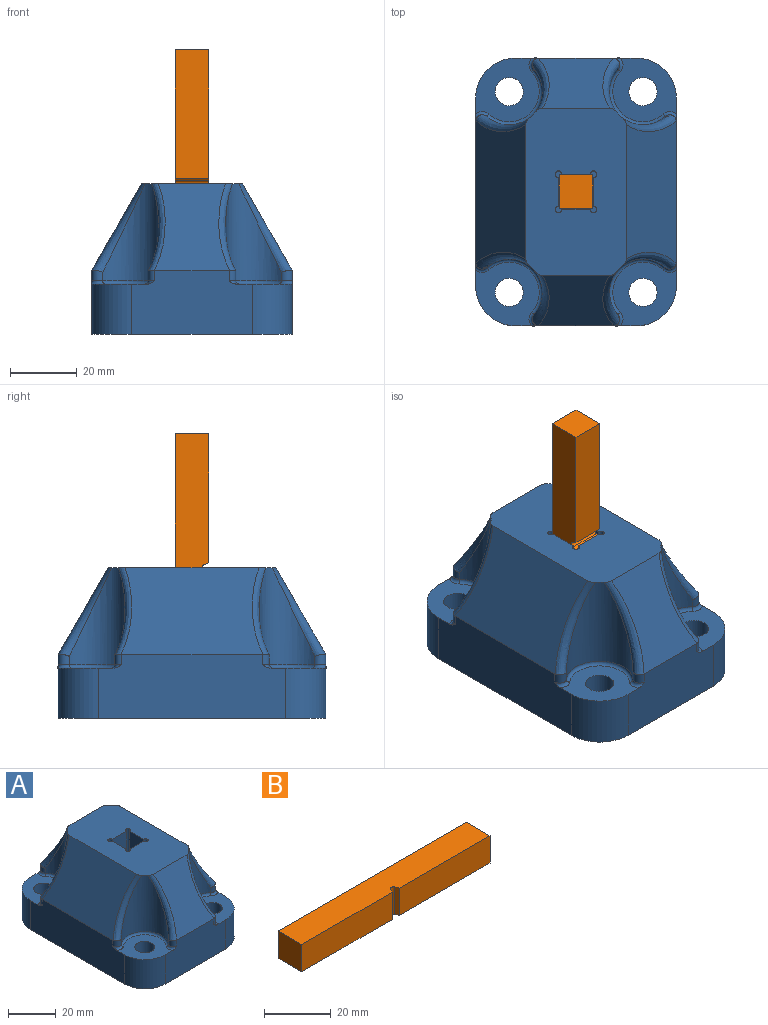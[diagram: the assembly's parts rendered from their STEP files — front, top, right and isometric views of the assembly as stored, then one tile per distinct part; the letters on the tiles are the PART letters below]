
ASSEMBLY  parts=2 mates=1
PART A: 63 faces, bbox 64.3x84.3x46.3 mm
  f0: plane 25.99x22.59mm, normal (0,0.87,0.5), area 532mm2, adj f10,f13,f35,f36,f39,f40
  f1: plane 42.59x25.99mm, normal (-0.87,0,0.5), area 1132mm2, adj f10,f11,f37,f38,f49,f50
  f2: cylinder r=12mm len=15mm, axis (0,0,-1), area 282.7mm2, adj f8,f11,f13,f33
  f3: plane 42.59x25.99mm, normal (0.87,0,0.5), area 1132mm2, adj f9,f10,f41,f42,f45,f46
  f4: cylinder r=12mm len=15mm, axis (0,0,1), area 282.7mm2, adj f8,f9,f13,f30
  f5: plane 25.99x22.59mm, normal (0,-0.87,0.5), area 532mm2, adj f10,f12,f43,f44,f47,f48
  f6: cylinder r=12mm len=15mm, axis (0,0,-1), area 282.7mm2, adj f8,f9,f12,f27
  f7: cylinder r=12mm len=15mm, axis (0,0,1), area 282.7mm2, adj f8,f11,f12,f24
  f8: plane 80x60mm, normal (0,0,-1), area 4454.7mm2, adj f2,f4,f6,f7,f9,f11,f12,f13
  f9: plane 56.31x19.33mm, normal (1,0,0), area 1010.9mm2, adj f3,f4,f6,f8,f27,f30,f41,f45
  f10: plane 50.19x30.19mm, normal (0,0,1), area 1346.6mm2, adj f0,f1,f3,f5,f14,f15,f16,f17
  f11: plane 56.31x19.33mm, normal (-1,0,0), area 1010.9mm2, adj f1,f2,f7,f8,f24,f33,f37,f49
  f12: plane 36.31x19.33mm, normal (0,-1,0), area 630.5mm2, adj f5,f6,f7,f8,f24,f27,f43,f47
  f13: plane 36.31x19.33mm, normal (0,1,0), area 630.5mm2, adj f0,f2,f4,f8,f30,f33,f35,f39
  f14: cylinder r=1mm len=40mm, axis (0,0,1), area 188.5mm2, adj f10,f15,f21,f22
  f15: plane 40x8.5mm, normal (1,0,0), area 340mm2, adj f10,f14,f16,f22
  f16: cylinder r=1mm len=40mm, axis (0,0,1), area 188.5mm2, adj f10,f15,f17,f22
  f17: plane 40x8.5mm, normal (0,1,0), area 340mm2, adj f10,f16,f18,f22
  f18: cylinder r=1mm len=40mm, axis (0,0,1), area 188.5mm2, adj f10,f17,f19,f22
  f19: plane 40x8.5mm, normal (-1,0,0), area 340mm2, adj f10,f18,f20,f22
  f20: cylinder r=1mm len=40mm, axis (0,0,1), area 188.5mm2, adj f10,f19,f21,f22
  f21: plane 40x8.5mm, normal (0,-1,0), area 340mm2, adj f10,f14,f20,f22
  f22: plane 12.5x12.5mm, normal (0,0,1), area 119.7mm2, adj f14,f15,f16,f17,f18,f19,f20,f21
  f23: cylinder r=4.2mm len=15mm, axis (0,0,1), area 395.8mm2, adj f8,f24
  f24: plane 19x19mm, normal (0,0,1), area 226.1mm2, adj f7,f11,f12,f23,f51,f52,f53
  f25: cylinder r=10mm len=29mm, axis (0,0,1), area 511.6mm2, adj f10,f47,f48,f49,f50,f52
  f26: cylinder r=4.2mm len=15mm, axis (0,0,1), area 395.8mm2, adj f8,f27
  f27: plane 19x19mm, normal (0,0,1), area 226.1mm2, adj f6,f9,f12,f26,f54,f55,f56
  f28: cylinder r=10mm len=29mm, axis (0,0,1), area 511.6mm2, adj f10,f43,f44,f45,f46,f55
  f29: cylinder r=4.2mm len=15mm, axis (0,0,1), area 395.8mm2, adj f8,f30
  f30: plane 19x19mm, normal (0,0,1), area 226.1mm2, adj f4,f9,f13,f29,f57,f58,f59
  f31: cylinder r=10mm len=29mm, axis (0,0,1), area 511.6mm2, adj f10,f39,f40,f41,f42,f58
  f32: cylinder r=4.2mm len=15mm, axis (0,0,1), area 395.8mm2, adj f8,f33
  f33: plane 19x19mm, normal (0,0,1), area 226.1mm2, adj f2,f11,f13,f32,f60,f61,f62
  f34: cylinder r=10mm len=29mm, axis (0,0,1), area 511.6mm2, adj f10,f35,f36,f37,f38,f61
  f35: cylinder r=2mm len=3.33mm, axis (0,0,1), area 13.7mm2, adj f0,f13,f34,f36,f60
  f36: bspline ~28.08x16.15mm, area 97.8mm2, adj f0,f10,f34,f35
  f37: cylinder r=2mm len=3.33mm, axis (0,0,1), area 13.7mm2, adj f1,f11,f34,f38,f62
  f38: bspline ~28.08x16.15mm, area 97.8mm2, adj f1,f10,f34,f37
  f39: cylinder r=2mm len=3.33mm, axis (0,0,1), area 13.7mm2, adj f0,f13,f31,f40,f59
  f40: bspline ~28.08x16.15mm, area 97.8mm2, adj f0,f10,f31,f39
  f41: cylinder r=2mm len=3.33mm, axis (0,0,1), area 13.7mm2, adj f3,f9,f31,f42,f57
  f42: bspline ~28.08x16.15mm, area 97.8mm2, adj f3,f10,f31,f41
  f43: cylinder r=2mm len=3.33mm, axis (0,0,1), area 13.7mm2, adj f5,f12,f28,f44,f54
  f44: bspline ~28.08x16.15mm, area 97.8mm2, adj f5,f10,f28,f43
  f45: cylinder r=2mm len=3.33mm, axis (0,0,1), area 13.7mm2, adj f3,f9,f28,f46,f56
  f46: bspline ~28.08x16.15mm, area 97.8mm2, adj f3,f10,f28,f45
  f47: cylinder r=2mm len=3.33mm, axis (0,0,1), area 13.7mm2, adj f5,f12,f25,f48,f53
  f48: bspline ~28.08x16.15mm, area 97.8mm2, adj f5,f10,f25,f47
  f49: cylinder r=2mm len=3.33mm, axis (0,0,1), area 13.7mm2, adj f1,f11,f25,f50,f51
  f50: bspline ~28.08x16.15mm, area 97.8mm2, adj f1,f10,f25,f49
  f51: torus R=3mm, axis (0,0,1), area 6.9mm2, adj f11,f24,f49,f52
  f52: torus R=9mm, axis (0,0,1), area 45.9mm2, adj f24,f25,f51,f53
  f53: torus R=3mm, axis (0,0,1), area 6.9mm2, adj f12,f24,f47,f52
  f54: torus R=3mm, axis (0,0,1), area 6.9mm2, adj f12,f27,f43,f55
  f55: torus R=9mm, axis (0,0,1), area 45.9mm2, adj f27,f28,f54,f56
  f56: torus R=3mm, axis (0,0,1), area 6.9mm2, adj f9,f27,f45,f55
  f57: torus R=3mm, axis (0,0,1), area 6.9mm2, adj f9,f30,f41,f58
  f58: torus R=9mm, axis (0,0,1), area 45.9mm2, adj f30,f31,f57,f59
  f59: torus R=3mm, axis (0,0,1), area 6.9mm2, adj f13,f30,f39,f58
  f60: torus R=3mm, axis (0,0,1), area 6.9mm2, adj f13,f33,f35,f61
  f61: torus R=9mm, axis (0,0,1), area 45.9mm2, adj f33,f34,f60,f62
  f62: torus R=3mm, axis (0,0,1), area 6.9mm2, adj f11,f33,f37,f61
PART B: 10 faces, bbox 80x10x10 mm
  f0: plane 10x1.38mm, normal (-0.92,-0.38,0), area 15mm2, adj f1,f7,f8,f9
  f1: plane 38.5x10mm, normal (0,-1,0), area 385mm2, adj f0,f2,f8,f9
  f2: plane 10x10mm, normal (1,0,0), area 100mm2, adj f1,f3,f8,f9
  f3: plane 80x10mm, normal (0,1,0), area 800mm2, adj f2,f4,f8,f9
  f4: plane 10x10mm, normal (-1,0,0), area 100mm2, adj f3,f5,f8,f9
  f5: plane 38.5x10mm, normal (0,-1,0), area 385mm2, adj f4,f6,f8,f9
  f6: plane 10x1.38mm, normal (0.92,-0.38,0), area 15mm2, adj f5,f7,f8,f9
  f7: cylinder r=1mm len=10mm, axis (0,0,-1), area 23.6mm2, adj f0,f6,f8,f9
  f8: plane 80x10mm, normal (0,0,1), area 795.8mm2, adj f0,f1,f2,f3,f4,f5,f6,f7
  f9: plane 80x10mm, normal (0,0,-1), area 795.8mm2, adj f0,f1,f2,f3,f4,f5,f6,f7
PLACE A at identity fixed
PLACE B rot(axis=(0,-1,0),90deg) t=(5,0,45)mm
MATE fastened B.f4 <-> A.f22  axis (0,0,-1) through (0,0,5)mm
